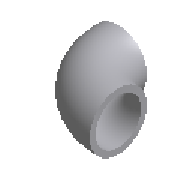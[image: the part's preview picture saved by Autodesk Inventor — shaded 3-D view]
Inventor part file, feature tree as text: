
AUTODESK INVENTOR PART (.ipt)
format: ipt  version: 2023.1 (Build 271208000, 208)  size: 190,976 bytes
history: native  units: mm (DEFAULTED — no unit token found)
features: other x4, sketch x2, sweep x1
ambient origin geometry x8: Origin, YZ Plane, XZ Plane, XY Plane, X Axis, Y Axis, Z Axis, Center Point
bodies: Solid1 (feature_tree)
feature tree (7):
  sweep  "Sweep1"
  other  "Work Point1"
  other  "Work Axis1"
  other  "Work Point2"
  other  "Work Axis2"
  sketch  "Sketch1"  dims[d0=93.2mm d1=101.6mm]
  sketch  "Sketch2"  dims[d2=88.9mm d3=90.0deg d4=88.9mm d5=0.0mm d6=0.0mm]
